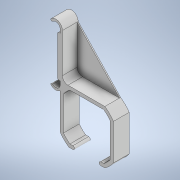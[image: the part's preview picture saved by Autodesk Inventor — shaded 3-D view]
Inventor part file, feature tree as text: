
AUTODESK INVENTOR PART (.ipt)
format: ipt  version: 2021 (Build 250183000, 183)  size: 191,488 bytes
history: native  units: mm
features: extrude x4, mirror x2, sketch x1, chamfer x1, boolean_combine x1, fillet x1
ambient origin geometry x8: Origin, YZ Plane, XZ Plane, XY Plane, X Axis, Y Axis, Z Axis, Center Point
bodies: Solid1 (feature_tree), Solid2 (feature_tree)
feature tree (10):
  sketch  "Sketch1"  dims[d0=42.25mm d1=52.25mm d2=42.25mm d3=26.125mm d5=21.125mm d6=3.0mm d7=3.0mm d8=3.0mm d9=3.0mm d10=3.0mm d11=10.0mm d12=45.0deg d13=18.75mm d14=25.875mm d15=4.0mm d17=2.0mm d18=2.5mm d19=14.25mm d20=0.0mm d21=21.125mm d22=14.25mm d23=0.0mm d24=1.0mm d25=0.0mm d26=5.0mm d28=1.0mm d29=2.0mm d30=45.0deg d31=14.25mm d32=0.0mm d33=16.317169mm d34=16.317169mm d35=21.875mm d36=21.875mm]
  extrude  "Extrusion1"  Depth=42.25mm
  mirror  "Mirror1"
  extrude  "Extrusion2"  Depth=26.125mm
  chamfer  "Chamfer1"  Distance=21.125mm
  mirror  "Mirror2"
  extrude  "Extrusion3"  Depth=3.0mm
  extrude  "Extrusion4"  Depth=3.0mm
  boolean_combine  "Combine1"
  fillet  "Fillet1"  Radius=3.0mm
